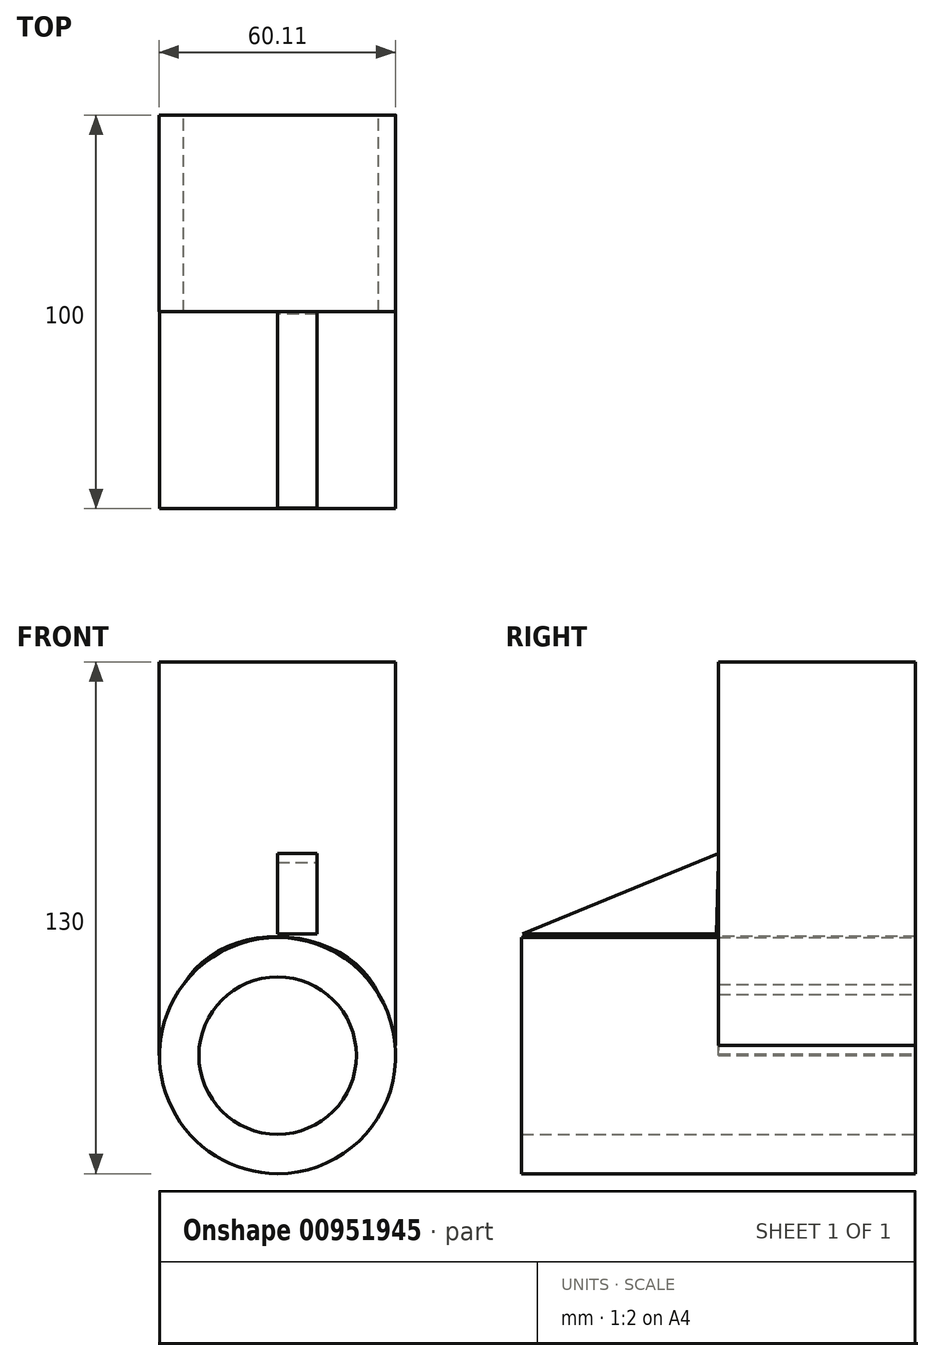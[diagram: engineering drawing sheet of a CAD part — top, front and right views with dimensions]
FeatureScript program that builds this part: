
annotation { "Feature Type Name" : "Feature", "Feature Type Description" : "" }
export const myFeature = defineFeature(function(context is Context, id is Id, definition is map)
    precondition{}
    {
        {
            var Q0;
            Q0=qCreatedBy(makeId("Front.planeOp"),FACE);
            var sketch = newSketch(context, id + "F0", { "sketchPlane" : qUnion([Q0])});
            skCircle(sketch, "E0", {"center": v(0, 0) * mm, "radius": 20 * mm});
            skCircle(sketch, "E1", {"center": v(0, 0) * mm, "radius": 30 * mm});
            skSolve(sketch);
        }
        {
            var Q0;
            Q0 = qSketchRegion(id + "F0", true);
            extrude(context, id + "F1", {"entities" : qUnion([Q0]), "depth" : 100 * mm, "offsetDistance" : 25 * mm});
        }
        {
            var Q0;
            Q0=qCreatedBy(makeId("Front.planeOp"),FACE);
            var sketch = newSketch(context, id + "F2", { "sketchPlane" : qUnion([Q0])});
            skLineSegment(sketch, "E2", {"start": v(-30.1, 0) * mm, "end": v(-30.1, 100) * mm});
            skLineSegment(sketch, "E3", {"start": v(-30.1, 100) * mm, "end": v(29.9, 100) * mm});
            skLineSegment(sketch, "E4", {"start": v(29.9, 100) * mm, "end": v(29.9, 0) * mm});
            skFitSpline(sketch, "E5", {"points": [v(-30.1, 0) * mm, v(-21.24, 21.74) * mm, v(0, 30.23) * mm, v(22.11, 21.08) * mm, v(29.9, 0) * mm], "startDerivative": vector(22.83, 96.36) * mm, "endDerivative": vector(17.74, -94.7) * mm});
            skSolve(sketch);
        }
        {
            var Q0;
            Q0 = qSketchRegion(id + "F2", true);
            extrude(context, id + "F3", {"entities" : qUnion([Q0]), "operationType" : NewBodyOperationType.ADD, "depth" : 50 * mm, "offsetDistance" : 25 * mm});
        }
        {
            var Q0;
            Q0=qCreatedBy(makeId("Right.planeOp"),FACE);
            var sketch = newSketch(context, id + "F4", { "sketchPlane" : qUnion([Q0])});
            skLineSegment(sketch, "E6", {"start": v(-50.55, 30.9) * mm, "end": v(-99.84, 30.9) * mm});
            skLineSegment(sketch, "E7", {"start": v(-99.84, 30.9) * mm, "end": v(-49.93, 51.42) * mm});
            skLineSegment(sketch, "E8", {"start": v(-49.93, 51.42) * mm, "end": v(-50.55, 30.9) * mm});
            skSolve(sketch);
        }
        {
            var Q0;
            Q0 = qSketchRegion(id + "F4", true);
            extrude(context, id + "F5", {"entities" : qUnion([Q0]), "operationType" : NewBodyOperationType.ADD, "depth" : 10 * mm, "offsetDistance" : 25 * mm});
        }
    });
